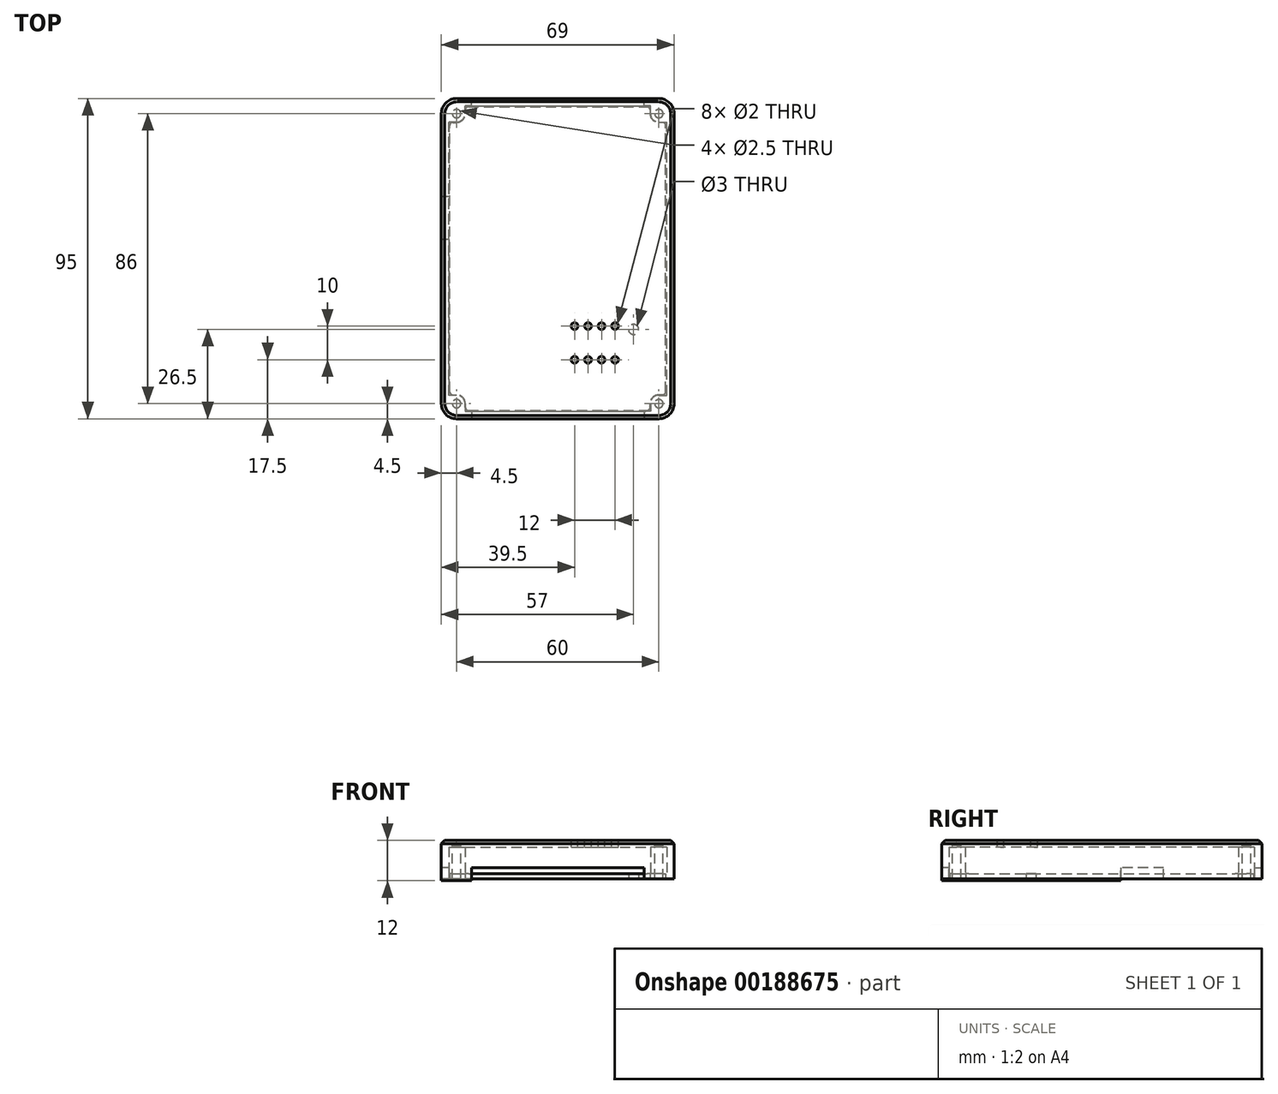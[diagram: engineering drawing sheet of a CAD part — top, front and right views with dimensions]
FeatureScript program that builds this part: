
annotation { "Feature Type Name" : "Feature", "Feature Type Description" : "" }
export const myFeature = defineFeature(function(context is Context, id is Id, definition is map)
    precondition{}
    {
        {
            var Q0;
            Q0=qCreatedBy(makeId("Top.planeOp"),FACE);
            var sketch = newSketch(context, id + "F0", { "sketchPlane" : qUnion([Q0])});
            skLineSegment(sketch, "E0.bottom", {"start": v(-30, -47.5) * mm, "end": v(30, -47.5) * mm});
            skLineSegment(sketch, "E0.top", {"start": v(-30, 47.5) * mm, "end": v(30, 47.5) * mm});
            skLineSegment(sketch, "E0.left", {"start": v(-34.5, -43) * mm, "end": v(-34.5, 43) * mm});
            skLineSegment(sketch, "E0.right", {"start": v(34.5, -43) * mm, "end": v(34.5, 43) * mm});
            skPoint(sketch, "E1.visualSharp", {"position": v(-34.5, 47.5) * mm});
            skArc(sketch, "E1.filletArc", {"start": v(-30, 47.5) * mm, "mid": v(-33.18, 46.18) * mm, "end": v(-34.5, 43) * mm});
            skPoint(sketch, "E2.visualSharp", {"position": v(34.5, 47.5) * mm});
            skArc(sketch, "E2.filletArc", {"start": v(34.5, 43) * mm, "mid": v(33.18, 46.18) * mm, "end": v(30, 47.5) * mm});
            skPoint(sketch, "E3.visualSharp", {"position": v(34.5, -47.5) * mm});
            skArc(sketch, "E3.filletArc", {"start": v(30, -47.5) * mm, "mid": v(33.18, -46.18) * mm, "end": v(34.5, -43) * mm});
            skPoint(sketch, "E4.visualSharp", {"position": v(-34.5, -47.5) * mm});
            skArc(sketch, "E4.filletArc", {"start": v(-34.5, -43) * mm, "mid": v(-33.18, -46.18) * mm, "end": v(-30, -47.5) * mm});
            skSolve(sketch);
        }
        {
            var Q0;
            Q0 = qSketchRegion(id + "F0", true);
            extrude(context, id + "F1", {"entities" : qUnion([Q0]), "depth" : 11.5 * mm});
        }
        {
            var Q0;
            Q0=makeQuery(id+"F1.opExtrude","SWEPT_FACE",FACE,{"disambiguationData":[OSD([sQuery(id+"F0.wireOp",EDGE,"E0.bottom")])]});
            var sketch = newSketch(context, id + "F2", { "sketchPlane" : qUnion([Q0])});
            skLineSegment(sketch, "E5.bottom", {"start": v(-25.6, 0) * mm, "end": v(25.6, 0) * mm});
            skLineSegment(sketch, "E5.top", {"start": v(-25.6, 3.4) * mm, "end": v(25.6, 3.4) * mm});
            skLineSegment(sketch, "E5.left", {"start": v(-25.6, 0) * mm, "end": v(-25.6, 3.4) * mm});
            skLineSegment(sketch, "E5.right", {"start": v(25.6, 0) * mm, "end": v(25.6, 3.4) * mm});
            skSolve(sketch);
        }
        {
            var Q0;
            Q0=makeQuery(id+"F1.opExtrude","SWEPT_FACE",FACE,{"disambiguationData":[OSD([sQuery(id+"F0.wireOp",EDGE,"E0.top")])]});
            var sketch = newSketch(context, id + "F3", { "sketchPlane" : qUnion([Q0])});
            skLineSegment(sketch, "E6.bottom", {"start": v(-25.6, 0) * mm, "end": v(25.6, 0) * mm});
            skLineSegment(sketch, "E6.top", {"start": v(-25.6, 3.4) * mm, "end": v(25.6, 3.4) * mm});
            skLineSegment(sketch, "E6.left", {"start": v(-25.6, 0) * mm, "end": v(-25.6, 3.4) * mm});
            skLineSegment(sketch, "E6.right", {"start": v(25.6, 0) * mm, "end": v(25.6, 3.4) * mm});
            skSolve(sketch);
        }
        {
            var Q0;
            Q0=makeQuery(id+"F1.opExtrude","SWEPT_FACE",FACE,{"disambiguationData":[OSD([sQuery(id+"F0.wireOp",EDGE,"E0.left")])]});
            var sketch = newSketch(context, id + "F4", { "sketchPlane" : qUnion([Q0])});
            skLineSegment(sketch, "E7.bottom", {"start": v(-18.35, 0) * mm, "end": v(-5.65, 0) * mm});
            skLineSegment(sketch, "E7.top", {"start": v(-18.35, 3.4) * mm, "end": v(-5.65, 3.4) * mm});
            skLineSegment(sketch, "E7.left", {"start": v(-18.35, 0) * mm, "end": v(-18.35, 3.4) * mm});
            skLineSegment(sketch, "E7.right", {"start": v(-5.65, 0) * mm, "end": v(-5.65, 3.4) * mm});
            skSolve(sketch);
        }
        {
            var Q0;
            Q0 = qSketchRegion(id + "F3", true);
            extrude(context, id + "F5", {"entities" : qUnion([Q0]), "operationType" : NewBodyOperationType.REMOVE, "oppositeDirection" : true, "depth" : 25 * mm});
        }
        {
            var Q0;
            Q0 = qSketchRegion(id + "F2", true);
            extrude(context, id + "F6", {"entities" : qUnion([Q0]), "operationType" : NewBodyOperationType.REMOVE, "oppositeDirection" : true, "depth" : 25 * mm});
        }
        {
            var Q0;
            Q0=makeQuery(id+"F4.imprint","IMPRINT",FACE,{"disambiguationData":[TD([[makeQuery(id+"F4.imprint","IMPRINT",EDGE,{"derivedFrom":sQuery(id+"F4.wireOp",EDGE,"E7.bottom")}),-1.0]])]});
            extrude(context, id + "F7", {"entities" : qUnion([Q0]), "operationType" : NewBodyOperationType.REMOVE, "oppositeDirection" : true, "depth" : 25 * mm, "offsetDistance" : 25 * mm});
        }
        {
            var Q0;
            Q0=makeQuery(id+"F1.opExtrude","CAP_FACE",FACE,{"disambiguationData":[OSD([sQuery(id+"F0.wireOp",EDGE,"E0.bottom"),sQuery(id+"F0.wireOp",EDGE,"E0.top"),sQuery(id+"F0.wireOp",EDGE,"E0.left"),sQuery(id+"F0.wireOp",EDGE,"E0.right"),sQuery(id+"F0.wireOp",EDGE,"E1.filletArc"),sQuery(id+"F0.wireOp",EDGE,"E2.filletArc"),sQuery(id+"F0.wireOp",EDGE,"E3.filletArc"),sQuery(id+"F0.wireOp",EDGE,"E4.filletArc")])],"isStart":true});
            var sketch = newSketch(context, id + "F8", { "sketchPlane" : qUnion([Q0])});
            skArc(sketch, "E8", {"start": v(-33.5, 43) * mm, "mid": v(-32.47, 45.47) * mm, "end": v(-30, 46.5) * mm});
            skArc(sketch, "E9", {"start": v(30, 46.5) * mm, "mid": v(32.47, 45.47) * mm, "end": v(33.5, 43) * mm});
            skArc(sketch, "E10", {"start": v(33.5, -43) * mm, "mid": v(32.47, -45.47) * mm, "end": v(30, -46.5) * mm});
            skArc(sketch, "E11", {"start": v(-33.5, -43) * mm, "mid": v(-32.47, -45.47) * mm, "end": v(-30, -46.5) * mm});
            skLineSegment(sketch, "E12", {"start": v(-30, -46.5) * mm, "end": v(30, -46.5) * mm});
            skLineSegment(sketch, "E13", {"start": v(-33.5, -43) * mm, "end": v(-33.5, 43) * mm});
            skLineSegment(sketch, "E14", {"start": v(-30, 46.5) * mm, "end": v(30, 46.5) * mm});
            skLineSegment(sketch, "E15", {"start": v(33.5, 43) * mm, "end": v(33.5, -43) * mm});
            skSolve(sketch);
        }
        {
            var Q0;
            Q0=makeQuery(id+"F8.imprint","IMPRINT",FACE,{"disambiguationData":[TD([[makeQuery(id+"F8.imprint","IMPRINT",EDGE,{"derivedFrom":sQuery(id+"F8.wireOp",EDGE,"E8")}),-1.0]])]});
            extrude(context, id + "F9", {"entities" : qUnion([Q0]), "operationType" : NewBodyOperationType.ADD, "depth" : 0.5 * mm});
        }
        {
            var Q0;
            Q0=makeQuery(id+"F9.opExtrude","CAP_FACE",FACE,{"disambiguationData":[OSD([sQuery(id+"F8.wireOp",EDGE,"E8"),sQuery(id+"F8.wireOp",EDGE,"E9"),sQuery(id+"F8.wireOp",EDGE,"E10"),sQuery(id+"F8.wireOp",EDGE,"E11"),sQuery(id+"F8.wireOp",EDGE,"E12"),sQuery(id+"F8.wireOp",EDGE,"E13"),sQuery(id+"F8.wireOp",EDGE,"E14"),sQuery(id+"F8.wireOp",EDGE,"E15")])],"isStart":false});
            var sketch = newSketch(context, id + "F10", { "sketchPlane" : qUnion([Q0])});
            skLineSegment(sketch, "E16.bottom", {"start": v(-32.3, 45.3) * mm, "end": v(32.3, 45.3) * mm, "construction": true});
            skLineSegment(sketch, "E16.top", {"start": v(-32.3, -45.3) * mm, "end": v(32.3, -45.3) * mm, "construction": true});
            skLineSegment(sketch, "E16.left", {"start": v(-32.3, 45.3) * mm, "end": v(-32.3, -45.3) * mm, "construction": true});
            skLineSegment(sketch, "E16.right", {"start": v(32.3, 45.3) * mm, "end": v(32.3, -45.3) * mm, "construction": true});
            skLineSegment(sketch, "E17", {"start": v(-27.5, 45.3) * mm, "end": v(27.5, 45.3) * mm});
            skLineSegment(sketch, "E18", {"start": v(-32.3, 40.5) * mm, "end": v(-32.3, -40.5) * mm});
            skLineSegment(sketch, "E19", {"start": v(-27.5, -45.3) * mm, "end": v(27.5, -45.3) * mm});
            skLineSegment(sketch, "E20", {"start": v(32.3, -40.5) * mm, "end": v(32.3, 40.5) * mm});
            skLineSegment(sketch, "E21", {"start": v(-27.5, 45.3) * mm, "end": v(-27.5, 43) * mm});
            skLineSegment(sketch, "E22", {"start": v(-32.3, 40.5) * mm, "end": v(-30, 40.5) * mm});
            skLineSegment(sketch, "E23", {"start": v(-32.3, -40.5) * mm, "end": v(-30, -40.5) * mm});
            skLineSegment(sketch, "E24", {"start": v(-27.5, -45.3) * mm, "end": v(-27.5, -43) * mm});
            skLineSegment(sketch, "E25", {"start": v(27.5, -45.3) * mm, "end": v(27.5, -43) * mm});
            skLineSegment(sketch, "E26", {"start": v(32.3, -40.5) * mm, "end": v(30, -40.5) * mm});
            skLineSegment(sketch, "E27", {"start": v(27.5, 45.3) * mm, "end": v(27.5, 43) * mm});
            skLineSegment(sketch, "E28", {"start": v(32.3, 40.5) * mm, "end": v(30, 40.5) * mm});
            skArc(sketch, "E29", {"start": v(27.5, 43) * mm, "mid": v(28.23, 41.23) * mm, "end": v(30, 40.5) * mm});
            skArc(sketch, "E30", {"start": v(-30, 40.5) * mm, "mid": v(-28.23, 41.23) * mm, "end": v(-27.5, 43) * mm});
            skArc(sketch, "E31", {"start": v(-30, -40.5) * mm, "mid": v(-28.23, -41.23) * mm, "end": v(-27.5, -43) * mm});
            skArc(sketch, "E32", {"start": v(27.5, -43) * mm, "mid": v(28.23, -41.23) * mm, "end": v(30, -40.5) * mm});
            skSolve(sketch);
        }
        {
            var Q0;
            Q0 = qSketchRegion(id + "F10", true);
            extrude(context, id + "F11", {"entities" : qUnion([Q0]), "operationType" : NewBodyOperationType.REMOVE, "depth" : -10 * mm});
        }
        {
            var Q0;
            Q0=makeQuery(id+"F1.opExtrude","CAP_EDGE",EDGE,{"disambiguationData":[OSD([sQuery(id+"F0.wireOp",EDGE,"E0.top")])],"isStart":false});
            var Q1;
            Q1=makeQuery(id+"F1.opExtrude","CAP_EDGE",EDGE,{"disambiguationData":[OSD([sQuery(id+"F0.wireOp",EDGE,"E1.filletArc")])],"isStart":false});
            var Q2;
            Q2=makeQuery(id+"F1.opExtrude","CAP_EDGE",EDGE,{"disambiguationData":[OSD([sQuery(id+"F0.wireOp",EDGE,"E0.left")])],"isStart":false});
            var Q3;
            Q3=makeQuery(id+"F1.opExtrude","CAP_EDGE",EDGE,{"disambiguationData":[OSD([sQuery(id+"F0.wireOp",EDGE,"E4.filletArc")])],"isStart":false});
            var Q4;
            Q4=makeQuery(id+"F1.opExtrude","CAP_EDGE",EDGE,{"disambiguationData":[OSD([sQuery(id+"F0.wireOp",EDGE,"E0.bottom")])],"isStart":false});
            var Q5;
            Q5=makeQuery(id+"F1.opExtrude","CAP_EDGE",EDGE,{"disambiguationData":[OSD([sQuery(id+"F0.wireOp",EDGE,"E3.filletArc")])],"isStart":false});
            var Q6;
            Q6=makeQuery(id+"F1.opExtrude","CAP_EDGE",EDGE,{"disambiguationData":[OSD([sQuery(id+"F0.wireOp",EDGE,"E0.right")])],"isStart":false});
            var Q7;
            Q7=makeQuery(id+"F1.opExtrude","CAP_EDGE",EDGE,{"disambiguationData":[OSD([sQuery(id+"F0.wireOp",EDGE,"E2.filletArc")])],"isStart":false});
            chamfer(context, id + "F12", {"entities" : qUnion([Q0, Q1, Q2, Q3, Q4, Q5, Q6, Q7]), "width" : 1 * mm, "tangentPropagation" : true});
        }
        {
            var Q0;
            Q0=makeQuery(id+"F1.opExtrude","CAP_FACE",FACE,{"disambiguationData":[OSD([sQuery(id+"F0.wireOp",EDGE,"E0.bottom"),sQuery(id+"F0.wireOp",EDGE,"E0.top"),sQuery(id+"F0.wireOp",EDGE,"E0.left"),sQuery(id+"F0.wireOp",EDGE,"E0.right"),sQuery(id+"F0.wireOp",EDGE,"E1.filletArc"),sQuery(id+"F0.wireOp",EDGE,"E2.filletArc"),sQuery(id+"F0.wireOp",EDGE,"E3.filletArc"),sQuery(id+"F0.wireOp",EDGE,"E4.filletArc")])],"isStart":false});
            var sketch = newSketch(context, id + "F13", { "sketchPlane" : qUnion([Q0])});
            skCircle(sketch, "E33", {"center": v(5, -30) * mm, "radius": 1 * mm});
            skCircle(sketch, "E34.1.0.0", {"center": v(9, -30) * mm, "radius": 1 * mm});
            skCircle(sketch, "E34.2.0.0", {"center": v(13, -30) * mm, "radius": 1 * mm});
            skCircle(sketch, "E34.3.0.0", {"center": v(17, -30) * mm, "radius": 1 * mm});
            skLineSegment(sketch, "E34.direction1", {"start": v(5, -30) * mm, "end": v(9, -30) * mm, "construction": true});
            skCircle(sketch, "E35.1.0.0", {"center": v(5, -20) * mm, "radius": 1 * mm});
            skCircle(sketch, "E35.1.0.1", {"center": v(9, -20) * mm, "radius": 1 * mm});
            skCircle(sketch, "E35.1.0.2", {"center": v(13, -20) * mm, "radius": 1 * mm});
            skCircle(sketch, "E35.1.0.3", {"center": v(17, -20) * mm, "radius": 1 * mm});
            skLineSegment(sketch, "E35.direction1", {"start": v(5, -30) * mm, "end": v(5, -20) * mm, "construction": true});
            skSolve(sketch);
        }
        {
            var Q0;
            Q0 = qSketchRegion(id + "F13", true);
            extrude(context, id + "F14", {"entities" : qUnion([Q0]), "operationType" : NewBodyOperationType.REMOVE, "endBound" : BoundingType.THROUGH_ALL, "oppositeDirection" : true, "depth" : 25 * mm});
        }
        {
            var Q0;
            Q0=qCreatedBy(makeId("Top.planeOp"),FACE);
            var sketch = newSketch(context, id + "F15", { "sketchPlane" : qUnion([Q0])});
            skLineSegment(sketch, "E36.bottom", {"start": v(-26.5, -45) * mm, "end": v(26.5, -45) * mm});
            skLineSegment(sketch, "E36.top", {"start": v(-26.5, 45) * mm, "end": v(26.5, 45) * mm});
            skLineSegment(sketch, "E36.left", {"start": v(-32, -39.5) * mm, "end": v(-32, 39.5) * mm});
            skLineSegment(sketch, "E36.right", {"start": v(32, -39.5) * mm, "end": v(32, 39.5) * mm});
            skLineSegment(sketch, "E37.top", {"start": v(-31.1, 40.4) * mm, "end": v(-30, 40.4) * mm});
            skLineSegment(sketch, "E37.right", {"start": v(-27.4, 44.1) * mm, "end": v(-27.4, 43) * mm});
            skLineSegment(sketch, "E38.top", {"start": v(31.1, 40.4) * mm, "end": v(30, 40.4) * mm});
            skLineSegment(sketch, "E38.right", {"start": v(27.4, 44.1) * mm, "end": v(27.4, 43) * mm});
            skLineSegment(sketch, "E39.top", {"start": v(31.1, -40.4) * mm, "end": v(30, -40.4) * mm});
            skLineSegment(sketch, "E39.right", {"start": v(27.4, -44.1) * mm, "end": v(27.4, -43) * mm});
            skLineSegment(sketch, "E40.top", {"start": v(-31.1, -40.4) * mm, "end": v(-30, -40.4) * mm});
            skLineSegment(sketch, "E40.right", {"start": v(-27.4, -44.1) * mm, "end": v(-27.4, -43) * mm});
            skPoint(sketch, "E41.orphan", {"position": v(-32, 45) * mm});
            skPoint(sketch, "E42.orphan", {"position": v(32, -45) * mm});
            skPoint(sketch, "E43.visualSharp", {"position": v(-27.4, 40.4) * mm});
            skArc(sketch, "E43.filletArc", {"start": v(-30, 40.4) * mm, "mid": v(-28.16, 41.16) * mm, "end": v(-27.4, 43) * mm});
            skPoint(sketch, "E44.visualSharp", {"position": v(27.4, 40.4) * mm});
            skArc(sketch, "E44.filletArc", {"start": v(27.4, 43) * mm, "mid": v(28.16, 41.16) * mm, "end": v(30, 40.4) * mm});
            skPoint(sketch, "E45.visualSharp", {"position": v(27.4, -40.4) * mm});
            skArc(sketch, "E45.filletArc", {"start": v(30, -40.4) * mm, "mid": v(28.16, -41.16) * mm, "end": v(27.4, -43) * mm});
            skPoint(sketch, "E46.visualSharp", {"position": v(-27.4, -40.4) * mm});
            skArc(sketch, "E46.filletArc", {"start": v(-27.4, -43) * mm, "mid": v(-28.16, -41.16) * mm, "end": v(-30, -40.4) * mm});
            skCircle(sketch, "E47", {"center": v(22.5, -21) * mm, "radius": 1.5 * mm});
            skPoint(sketch, "E48.visualSharp", {"position": v(-32, 40.4) * mm});
            skArc(sketch, "E48.filletArc", {"start": v(-31.1, 40.4) * mm, "mid": v(-31.74, 40.14) * mm, "end": v(-32, 39.5) * mm});
            skPoint(sketch, "E49.visualSharp", {"position": v(-27.4, 45) * mm});
            skArc(sketch, "E49.filletArc", {"start": v(-26.5, 45) * mm, "mid": v(-27.14, 44.74) * mm, "end": v(-27.4, 44.1) * mm});
            skPoint(sketch, "E50.visualSharp", {"position": v(27.4, 45) * mm});
            skArc(sketch, "E50.filletArc", {"start": v(27.4, 44.1) * mm, "mid": v(27.14, 44.74) * mm, "end": v(26.5, 45) * mm});
            skPoint(sketch, "E51.visualSharp", {"position": v(32, 40.4) * mm});
            skArc(sketch, "E51.filletArc", {"start": v(32, 39.5) * mm, "mid": v(31.74, 40.14) * mm, "end": v(31.1, 40.4) * mm});
            skPoint(sketch, "E52.visualSharp", {"position": v(32, -40.4) * mm});
            skArc(sketch, "E52.filletArc", {"start": v(31.1, -40.4) * mm, "mid": v(31.74, -40.14) * mm, "end": v(32, -39.5) * mm});
            skPoint(sketch, "E53.visualSharp", {"position": v(27.4, -45) * mm});
            skArc(sketch, "E53.filletArc", {"start": v(26.5, -45) * mm, "mid": v(27.14, -44.74) * mm, "end": v(27.4, -44.1) * mm});
            skPoint(sketch, "E54.visualSharp", {"position": v(-32, -40.4) * mm});
            skArc(sketch, "E54.filletArc", {"start": v(-32, -39.5) * mm, "mid": v(-31.74, -40.14) * mm, "end": v(-31.1, -40.4) * mm});
            skPoint(sketch, "E55.visualSharp", {"position": v(-27.4, -45) * mm});
            skArc(sketch, "E55.filletArc", {"start": v(-27.4, -44.1) * mm, "mid": v(-27.14, -44.74) * mm, "end": v(-26.5, -45) * mm});
            skSolve(sketch);
        }
        {
            var Q0;
            Q0=makeQuery(id+"F15.imprint","IMPRINT",FACE,{"disambiguationData":[TD([[makeQuery(id+"F15.imprint","IMPRINT",EDGE,{"derivedFrom":sQuery(id+"F15.wireOp",EDGE,"E36.bottom")}),1.0]])]});
            extrude(context, id + "F16", {"entities" : qUnion([Q0]), "depth" : 1.6 * mm});
        }
        {
            var Q0;
            Q0=sQuery(id+"F10.wireOp",VERTEX,"E30.center");
            var Q1;
            Q1=sQuery(id+"F10.wireOp",VERTEX,"E29.center");
            var Q2;
            Q2=sQuery(id+"F10.wireOp",VERTEX,"E32.center");
            var Q3;
            Q3=sQuery(id+"F10.wireOp",VERTEX,"E31.center");
            var Q4;
            Q4=makeQuery(id+"F1.opExtrude","SWEPT_BODY",BODY,{"disambiguationData":[OSD([sQuery(id+"F0.wireOp",EDGE,"E0.bottom"),sQuery(id+"F0.wireOp",EDGE,"E0.top"),sQuery(id+"F0.wireOp",EDGE,"E0.left"),sQuery(id+"F0.wireOp",EDGE,"E0.right"),sQuery(id+"F0.wireOp",EDGE,"E1.filletArc"),sQuery(id+"F0.wireOp",EDGE,"E2.filletArc"),sQuery(id+"F0.wireOp",EDGE,"E3.filletArc"),sQuery(id+"F0.wireOp",EDGE,"E4.filletArc")])]});
            hole(context, id + "F17", {"style" : HoleStyle.SIMPLE, "endStyle" : HoleEndStyle.BLIND, "holeDiameter" : 2.5 * mm, "majorDiameter" : 5 * mm, "holeDepth" : 10 * mm, "tappedDepth" : 12 * mm, "tapClearance" : 3, "locations" : qUnion([Q0, Q1, Q2, Q3]), "scope" : qUnion([Q4]), "startStyle" : HoleStartStyle.PART});
        }
    });
